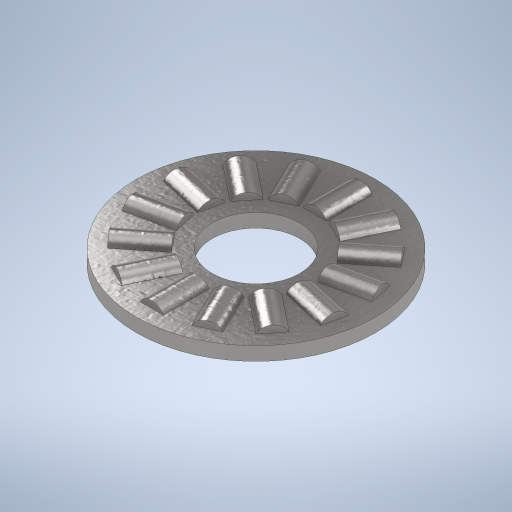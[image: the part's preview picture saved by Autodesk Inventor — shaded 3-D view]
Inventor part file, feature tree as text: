
AUTODESK INVENTOR PART (.ipt)
format: ipt  version: 2024 (Build 280153000, 153)  size: 431,616 bytes
history: native  units: in
note: dims shown in document units (in); Inventor stores cm internally (conversion verified against a paired STEP export)
features: other x13, revolve x1, pattern_circular x1
ambient origin geometry x8: Origin, YZ Plane, XZ Plane, XY Plane, X Axis, Y Axis, Z Axis, Center Point
bodies: Solid1 (feature_tree), Solid2 (feature_tree), Solid3 (feature_tree), Solid4 (feature_tree), Solid5 (feature_tree), Solid6 (feature_tree), Solid7 (feature_tree), Solid8 (feature_tree), Solid9 (feature_tree), Solid10 (feature_tree), Solid11 (feature_tree), Solid12 (feature_tree), Solid13 (feature_tree), Solid14 (feature_tree), Solid15 (feature_tree)
feature tree (15):
  revolve  "Revolve2"  [1 undecoded]
  other  "CirPattern1[1]"
  other  "CirPattern1[2]"
  other  "CirPattern1[3]"
  other  "CirPattern1[4]"
  other  "CirPattern1[5]"
  other  "CirPattern1[6]"
  other  "CirPattern1[7]"
  other  "CirPattern1[8]"
  other  "CirPattern1[9]"
  other  "CirPattern1[10]"
  other  "CirPattern1[11]"
  other  "CirPattern1[12]"
  other  "CirPattern1[13]"
  pattern_circular  "CirPattern2"
note: 1 required parameter value undecoded (feature->parameter linkage not recoverable at this tier; creation-order binding heuristic only, values carry confidence <= 0.55)
